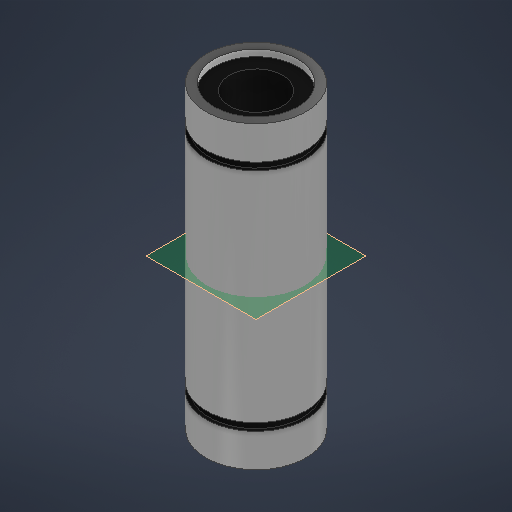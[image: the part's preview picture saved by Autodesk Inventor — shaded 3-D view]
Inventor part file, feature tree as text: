
AUTODESK INVENTOR PART (.ipt)
format: ipt  version: 2025.1 (Build 291241000, 241)  size: 254,976 bytes
history: native  units: mm
features: extrude x4, sketch x1, plane x1, mirror x1
ambient origin geometry x8: Origin, YZ Plane, XZ Plane, XY Plane, X Axis, Y Axis, Z Axis, Center Point
bodies: Solid1 (feature_tree)
feature tree (7):
  sketch  "Sketch1"  dims[d0=8.0mm d1=15.0mm d2=12.5mm d3=45.0mm d4=0.0mm d5=32.75mm d6=0.0mm d7=5.0mm d8=0.0mm d11=1.0mm d12=0.0mm d13=0.5mm]
  extrude  "Extrusion1"  Depth=1.0mm
  plane  "Work Plane1"
  extrude  "Extrusion2"  Depth=1.0mm
  extrude  "Extrusion3"  Depth=45.0mm TaperAngle=0.0deg
  extrude  "Extrusion5"  Depth=32.75mm TaperAngle=0.0deg
  mirror  "Mirror1"
